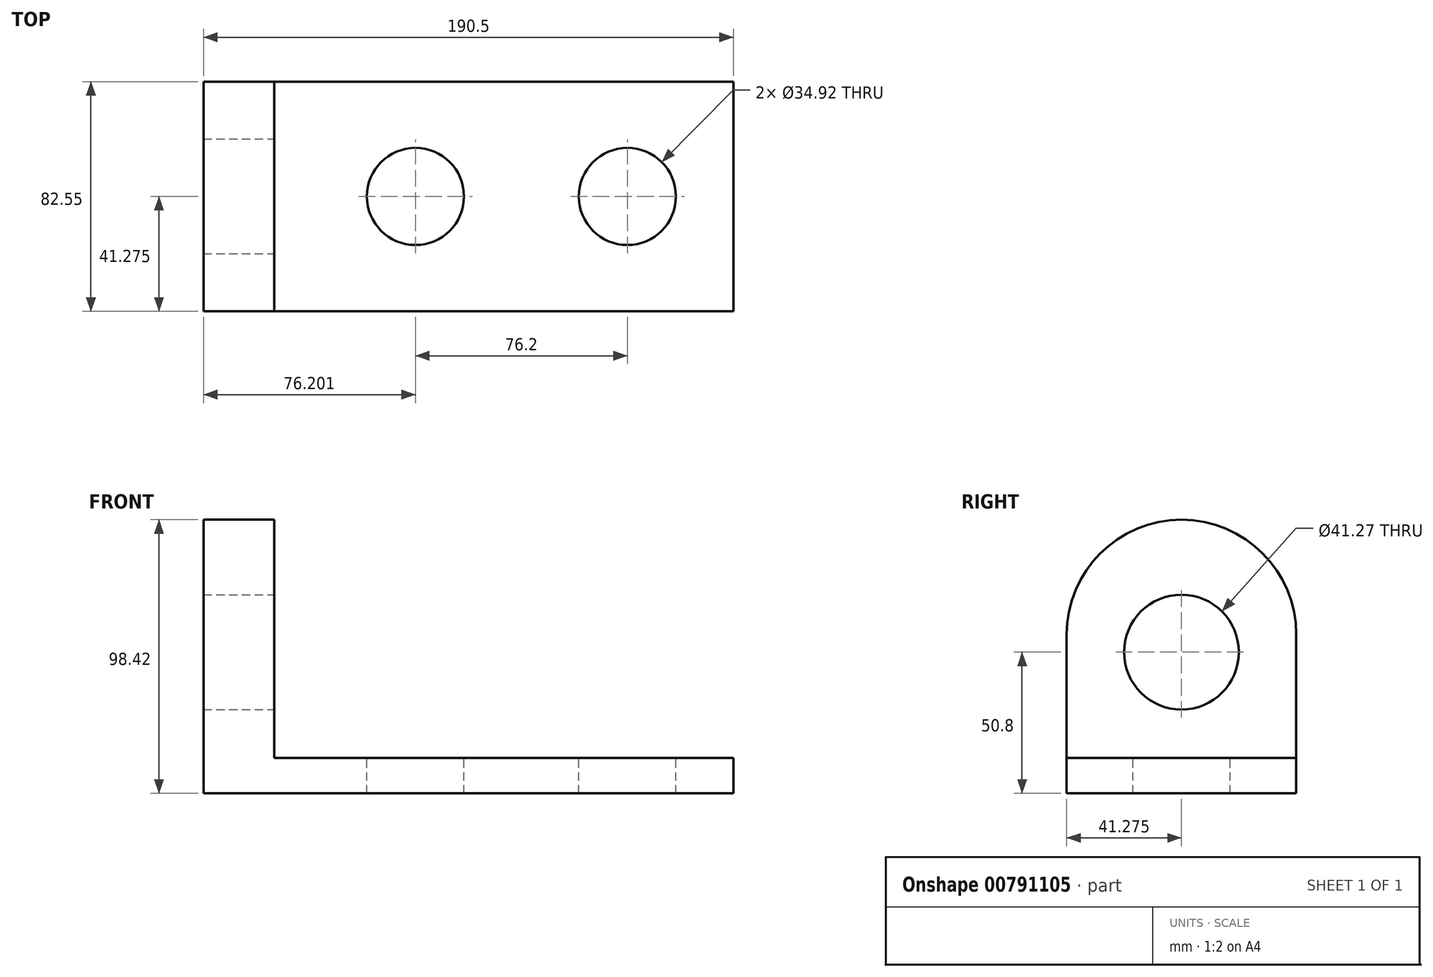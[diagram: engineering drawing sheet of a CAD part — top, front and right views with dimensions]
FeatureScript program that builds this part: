
annotation { "Feature Type Name" : "Feature", "Feature Type Description" : "" }
export const myFeature = defineFeature(function(context is Context, id is Id, definition is map)
    precondition{}
    {
        {
            var Q0;
            Q0=qCreatedBy(makeId("Front.planeOp"),FACE);
            var sketch = newSketch(context, id + "F0", { "sketchPlane" : qUnion([Q0])});
            skLineSegment(sketch, "E0", {"start": v(-76, 0) * mm, "end": v(114.5, 0) * mm});
            skLineSegment(sketch, "E1", {"start": v(114.5, 0) * mm, "end": v(114.5, 12.7) * mm});
            skLineSegment(sketch, "E2", {"start": v(114.5, 12.7) * mm, "end": v(-50.6, 12.7) * mm});
            skLineSegment(sketch, "E3", {"start": v(-76, 0) * mm, "end": v(-76, 101.6) * mm});
            skLineSegment(sketch, "E4", {"start": v(-76, 101.6) * mm, "end": v(-50.6, 101.6) * mm});
            skLineSegment(sketch, "E5", {"start": v(-50.6, 101.6) * mm, "end": v(-50.6, 6.4) * mm});
            skSolve(sketch);
        }
        {
            var Q0;
            Q0 = qSketchRegion(id + "F0", true);
            extrude(context, id + "F1", {"entities" : qUnion([Q0]), "oppositeDirection" : true, "depth" : 82.55 * mm, "offsetDistance" : 25.4 * mm});
        }
        {
            var Q0;
            Q0=makeQuery(id+"F1.opExtrude","SWEPT_FACE",FACE,{"disambiguationData":[OSD([sQuery(id+"F0.wireOp",EDGE,"E2")])]});
            var sketch = newSketch(context, id + "F2", { "sketchPlane" : qUnion([Q0])});
            skCircle(sketch, "E6", {"center": v(76.4, 41.28) * mm, "radius": 17.46 * mm});
            skPoint(sketch, "E7.endSnap0", {"position": v(31.94, 82.55) * mm});
            skCircle(sketch, "E8", {"center": v(0.2, 41.28) * mm, "radius": 17.46 * mm, "construction": true});
            skCircle(sketch, "E9", {"center": v(0.2, 41.28) * mm, "radius": 17.46 * mm});
            skSolve(sketch);
        }
        {
            var Q0;
            Q0=makeQuery(id+"F2.imprint","IMPRINT",FACE,{"disambiguationData":[TD([[makeQuery(id+"F2.imprint","IMPRINT",EDGE,{"derivedFrom":sQuery(id+"F2.wireOp",EDGE,"E9")}),1.0]])]});
            var Q1;
            Q1=makeQuery(id+"F2.imprint","IMPRINT",FACE,{"disambiguationData":[TD([[makeQuery(id+"F2.imprint","IMPRINT",EDGE,{"derivedFrom":sQuery(id+"F2.wireOp",EDGE,"E6")}),1.0]])]});
            extrude(context, id + "F3", {"entities" : qUnion([Q0, Q1]), "operationType" : NewBodyOperationType.REMOVE, "oppositeDirection" : true, "depth" : 25.4 * mm, "offsetDistance" : 25.4 * mm});
        }
        {
            var Q0;
            Q0=makeQuery(id+"F1.opExtrude","SWEPT_FACE",FACE,{"disambiguationData":[OSD([sQuery(id+"F0.wireOp",EDGE,"E3")])]});
            var sketch = newSketch(context, id + "F4", { "sketchPlane" : qUnion([Q0])});
            skLineSegment(sketch, "E10", {"start": v(-82.55, 0) * mm, "end": v(-82.55, 57.15) * mm, "construction": true});
            skArc(sketch, "E11", {"start": v(0, 57.15) * mm, "mid": v(-41.28, 98.42) * mm, "end": v(-82.55, 57.15) * mm});
            skSolve(sketch);
        }
        {
            var Q0;
            {var subQ0=sQuery(id+"F4.wireOp",EDGE,"E11");Q0=makeQuery(id+"F4.imprint","IMPRINT",FACE,{"disambiguationData":[TD([[makeQuery(id+"F4.imprint","IMPRINT",EDGE,{"derivedFrom":subQ0}),-1.0]])]});}
            extrude(context, id + "F5", {"entities" : qUnion([Q0]), "operationType" : NewBodyOperationType.REMOVE, "oppositeDirection" : true, "depth" : 25.4 * mm, "offsetDistance" : 25.4 * mm});
        }
        {
            var Q0;
            Q0=makeQuery(id+"F1.opExtrude","SWEPT_FACE",FACE,{"disambiguationData":[OSD([sQuery(id+"F0.wireOp",EDGE,"E5")])]});
            var sketch = newSketch(context, id + "F6", { "sketchPlane" : qUnion([Q0])});
            skLineSegment(sketch, "E12", {"start": v(0, 12.7) * mm, "end": v(41.28, 12.7) * mm, "construction": true});
            skLineSegment(sketch, "E13", {"start": v(41.28, 12.7) * mm, "end": v(41.28, 50.8) * mm, "construction": true});
            skCircle(sketch, "E14", {"center": v(41.28, 50.8) * mm, "radius": 20.64 * mm});
            skSolve(sketch);
        }
        {
            var Q0;
            Q0=makeQuery(id+"F6.imprint","IMPRINT",FACE,{"disambiguationData":[TD([[makeQuery(id+"F6.imprint","IMPRINT",EDGE,{"derivedFrom":sQuery(id+"F6.wireOp",EDGE,"E14")}),1.0]])]});
            extrude(context, id + "F7", {"entities" : qUnion([Q0]), "operationType" : NewBodyOperationType.REMOVE, "oppositeDirection" : true, "depth" : 50.8 * mm, "offsetDistance" : 25.4 * mm});
        }
    });
